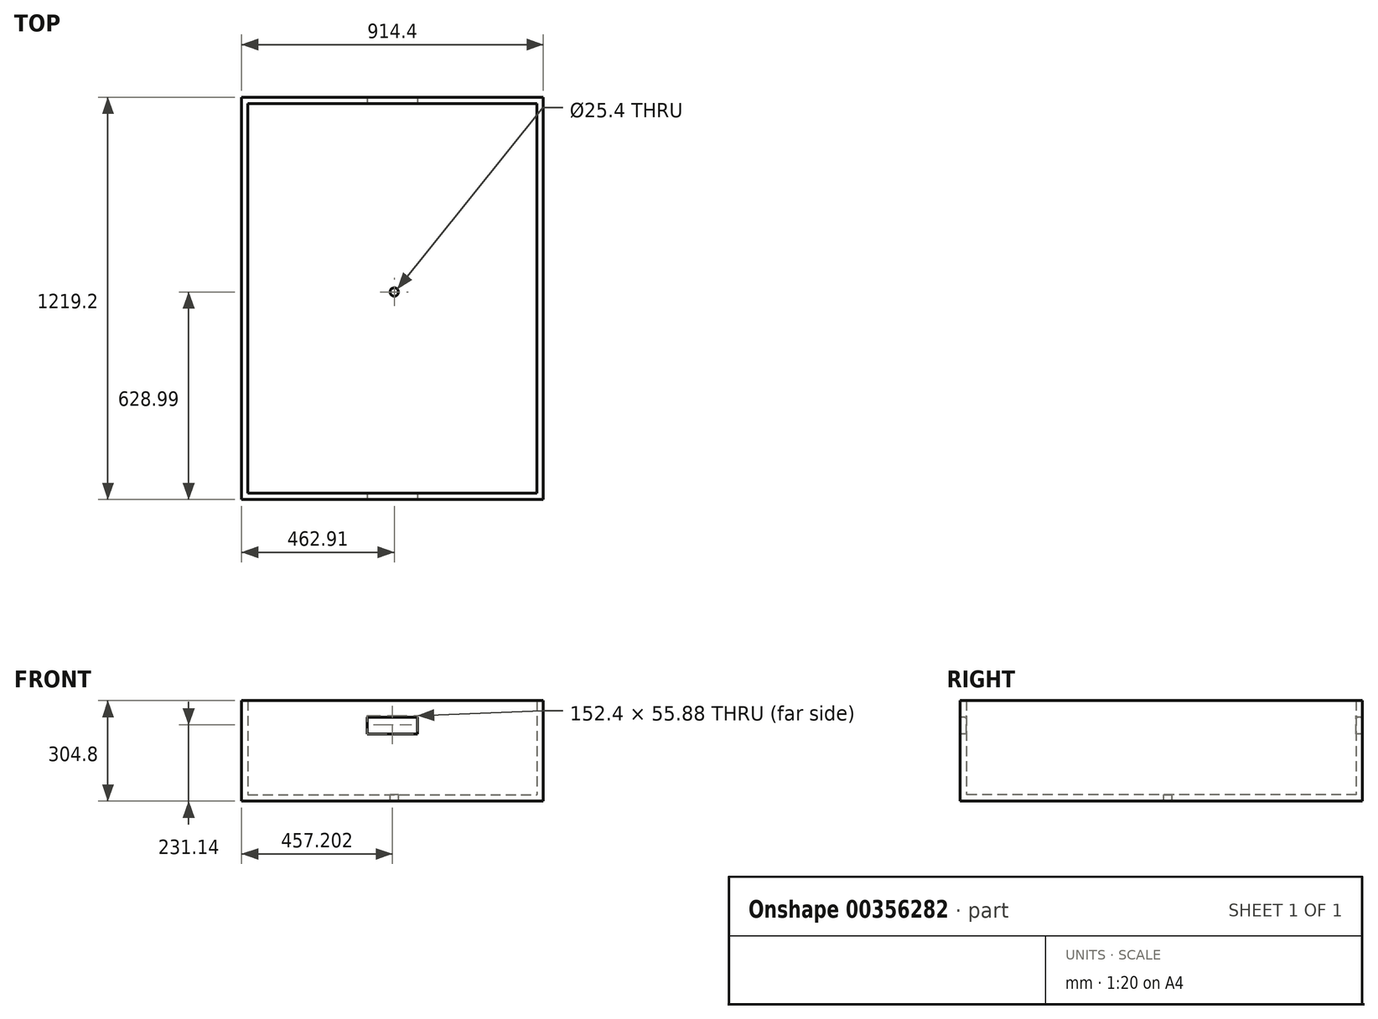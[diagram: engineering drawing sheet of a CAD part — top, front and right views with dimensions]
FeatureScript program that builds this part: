
annotation { "Feature Type Name" : "Feature", "Feature Type Description" : "" }
export const myFeature = defineFeature(function(context is Context, id is Id, definition is map)
    precondition{}
    {
        {
            var Q0;
            Q0=qCreatedBy(makeId("Top.planeOp"),FACE);
            var sketch = newSketch(context, id + "F0", { "sketchPlane" : qUnion([Q0])});
            skLineSegment(sketch, "E0.bottom", {"start": v(-462.9, 590.21) * mm, "end": v(451.5, 590.21) * mm});
            skLineSegment(sketch, "E0.top", {"start": v(-462.9, -628.99) * mm, "end": v(451.5, -628.99) * mm});
            skLineSegment(sketch, "E0.left", {"start": v(-462.9, 590.21) * mm, "end": v(-462.9, -628.99) * mm});
            skLineSegment(sketch, "E0.right", {"start": v(451.5, 590.21) * mm, "end": v(451.5, -628.99) * mm});
            skSolve(sketch);
        }
        {
            var Q0;
            Q0=makeQuery(id+"F0.imprint","IMPRINT",FACE,{"disambiguationData":[TD([[makeQuery(id+"F0.imprint","IMPRINT",EDGE,{"derivedFrom":sQuery(id+"F0.wireOp",EDGE,"E0.bottom")}),-1.0]])]});
            extrude(context, id + "F1", {"entities" : qUnion([Q0]), "depth" : 304.8 * mm});
        }
        {
            var Q0;
            Q0=makeQuery(id+"F1.opExtrude","CAP_FACE",FACE,{"disambiguationData":[OSD([sQuery(id+"F0.wireOp",EDGE,"E0.bottom"),sQuery(id+"F0.wireOp",EDGE,"E0.top"),sQuery(id+"F0.wireOp",EDGE,"E0.left"),sQuery(id+"F0.wireOp",EDGE,"E0.right")])],"isStart":false});
            shell(context, id + "F2", {"entities" : qUnion([Q0]), "thickness" : 19.05 * mm});
        }
        {
            var Q0;
            Q0=makeQuery(id+"F1.opExtrude","SWEPT_FACE",FACE,{"disambiguationData":[OSD([sQuery(id+"F0.wireOp",EDGE,"E0.top")])]});
            var sketch = newSketch(context, id + "F3", { "sketchPlane" : qUnion([Q0])});
            skLineSegment(sketch, "E1.bottom", {"start": v(-81.9, 254) * mm, "end": v(70.5, 254) * mm});
            skLineSegment(sketch, "E1.top", {"start": v(-81.9, 203.2) * mm, "end": v(70.5, 203.2) * mm});
            skLineSegment(sketch, "E1.left", {"start": v(-81.9, 254) * mm, "end": v(-81.9, 203.2) * mm});
            skLineSegment(sketch, "E1.right", {"start": v(70.5, 254) * mm, "end": v(70.5, 203.2) * mm});
            skSolve(sketch);
        }
        {
            var Q0;
            Q0=makeQuery(id+"F3.imprint","IMPRINT",FACE,{"disambiguationData":[TD([[makeQuery(id+"F3.imprint","IMPRINT",EDGE,{"derivedFrom":sQuery(id+"F3.wireOp",EDGE,"E1.bottom")}),-1.0]])]});
            extrude(context, id + "F4", {"entities" : qUnion([Q0]), "operationType" : NewBodyOperationType.REMOVE, "oppositeDirection" : true, "depth" : 1280.16 * mm});
        }
        {
            var Q0;
            Q0=makeQuery(id+"F4.boolean.opBoolean","INTERSECT",EDGE,{"derivedFrom":[makeQuery(id+"F2.opShell","OFFSET_FACE",FACE,{"disambiguationData":[OSD([sQuery(id+"F0.wireOp",EDGE,"E0.top")])]}),makeQuery(id+"F4.opExtrude","SWEPT_FACE",FACE,{"disambiguationData":[OSD([sQuery(id+"F3.wireOp",EDGE,"E1.bottom")])]})]});
            var Q1;
            Q1=makeQuery(id+"F4.boolean.opBoolean","COPY",EDGE,{"derivedFrom":makeQuery(id+"F4.opExtrude","CAP_EDGE",EDGE,{"disambiguationData":[OSD([sQuery(id+"F3.wireOp",EDGE,"E1.bottom")])],"isStart":true})});
            var Q2;
            Q2=makeQuery(id+"F4.boolean.opBoolean","INTERSECT",EDGE,{"derivedFrom":[makeQuery(id+"F2.opShell","OFFSET_FACE",FACE,{"disambiguationData":[OSD([sQuery(id+"F0.wireOp",EDGE,"E0.bottom")])]}),makeQuery(id+"F4.opExtrude","SWEPT_FACE",FACE,{"disambiguationData":[OSD([sQuery(id+"F3.wireOp",EDGE,"E1.bottom")])]})]});
            var Q3;
            Q3=makeQuery(id+"F4.boolean.opBoolean","INTERSECT",EDGE,{"derivedFrom":[makeQuery(id+"F1.opExtrude","SWEPT_FACE",FACE,{"disambiguationData":[OSD([sQuery(id+"F0.wireOp",EDGE,"E0.bottom")])]}),makeQuery(id+"F4.opExtrude","SWEPT_FACE",FACE,{"disambiguationData":[OSD([sQuery(id+"F3.wireOp",EDGE,"E1.bottom")])]})]});
            fillet(context, id + "F5", {"entities" : qUnion([Q0, Q1, Q2, Q3]), "radius" : 5.08 * mm, "tangentPropagation" : true, "allowEdgeOverflow" : false});
        }
        {
            var Q0;
            Q0=makeQuery(id+"F2.opShell","OFFSET_FACE",FACE,{"disambiguationData":[OSD([sQuery(id+"F0.wireOp",EDGE,"E0.bottom"),sQuery(id+"F0.wireOp",EDGE,"E0.top"),sQuery(id+"F0.wireOp",EDGE,"E0.left"),sQuery(id+"F0.wireOp",EDGE,"E0.right")])]});
            var sketch = newSketch(context, id + "F6", { "sketchPlane" : qUnion([Q0])});
            skCircle(sketch, "E2", {"center": v(0, 0) * mm, "radius": 12.7 * mm});
            skSolve(sketch);
        }
        {
            var Q0;
            Q0=makeQuery(id+"F6.imprint","IMPRINT",FACE,{"disambiguationData":[TD([[makeQuery(id+"F6.imprint","IMPRINT",EDGE,{"derivedFrom":sQuery(id+"F6.wireOp",EDGE,"E2")}),1.0]])]});
            var Q1;
            Q1=sQuery(id+"F6.wireOp",EDGE,"E2");
            extrude(context, id + "F7", {"entities" : qUnion([Q0]), "operationType" : NewBodyOperationType.REMOVE, "surfaceEntities" : qUnion([Q1]), "oppositeDirection" : true, "depth" : 25.4 * mm});
        }
    });
